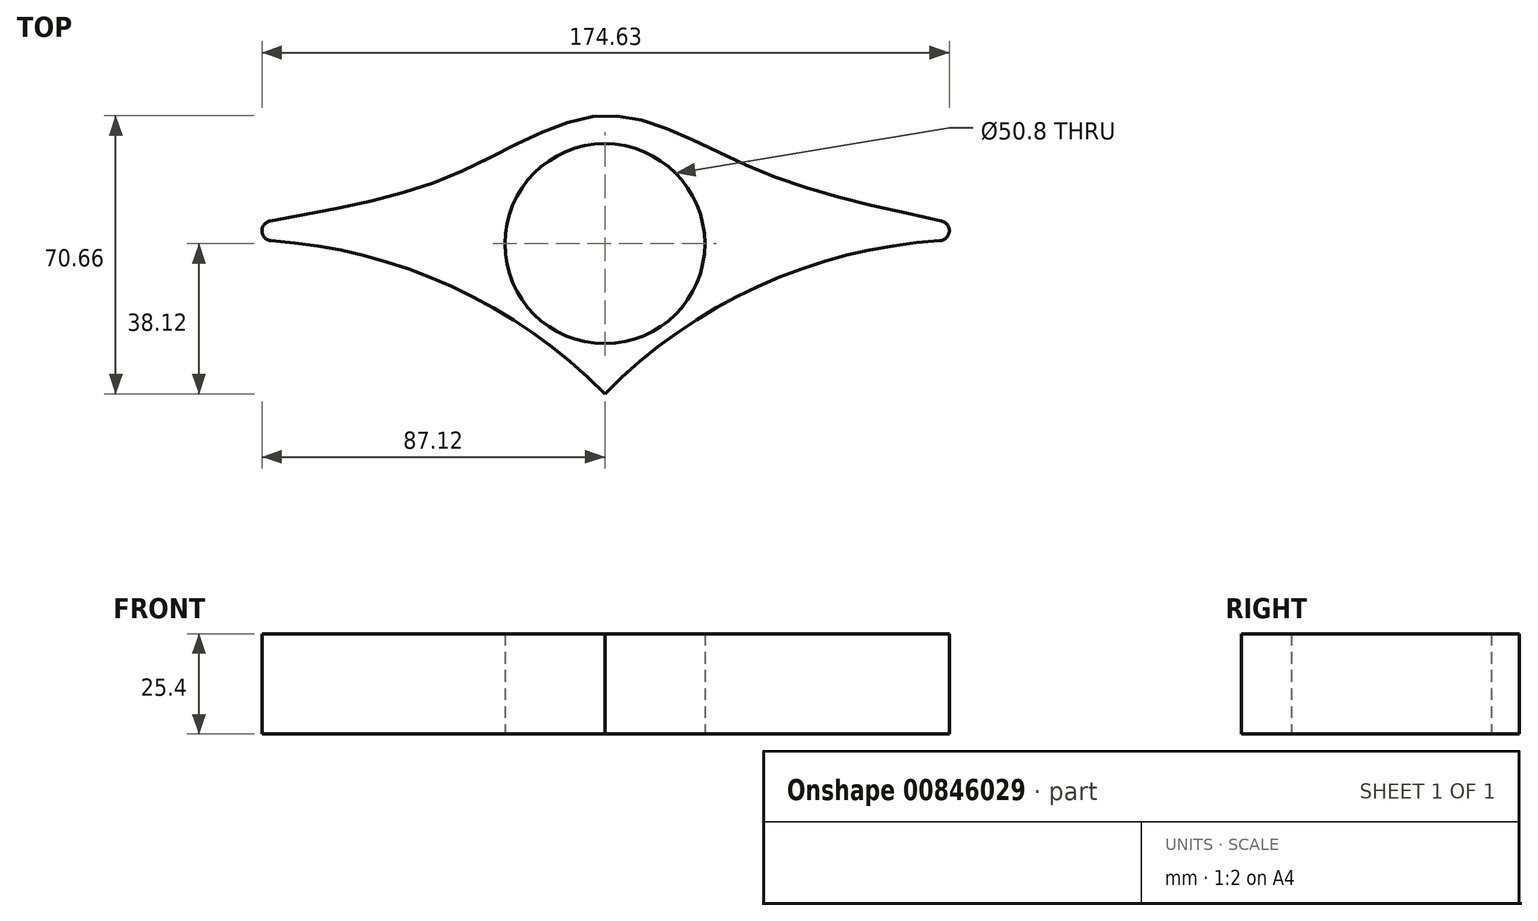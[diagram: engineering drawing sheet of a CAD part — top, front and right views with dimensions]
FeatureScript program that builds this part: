
annotation { "Feature Type Name" : "Feature", "Feature Type Description" : "" }
export const myFeature = defineFeature(function(context is Context, id is Id, definition is map)
    precondition{}
    {
        {
            var Q0;
            Q0=qCreatedBy(makeId("Top.planeOp"),FACE);
            var sketch = newSketch(context, id + "F0", { "sketchPlane" : qUnion([Q0])});
            skPoint(sketch, "E0.middle", {"position": v(0, 0) * mm});
            skCircle(sketch, "E1", {"center": v(0, 0) * mm, "radius": 25.4 * mm});
            skPoint(sketch, "E0.bottom.start.orphan", {"position": v(-220.64, 111.79) * mm});
            skPoint(sketch, "E2.orphan", {"position": v(220.64, 111.79) * mm});
            skArc(sketch, "E3", {"start": v(0, -38.12) * mm, "mid": v(-50.5, -6.2) * mm, "end": v(-109.93, 0) * mm});
            skArc(sketch, "E4.MirrorCS", {"start": v(0, -38.12) * mm, "mid": v(50.5, -6.2) * mm, "end": v(109.93, 0) * mm});
            skFitSpline(sketch, "E5", {"points": [v(-109.93, 0) * mm, v(-42.7, 15.8) * mm, v(0, 32.52) * mm, v(41.55, 17.64) * mm, v(109.93, 0) * mm], "startDerivative": vector(264.5, 77.18) * mm, "endDerivative": vector(256.83, -69.23) * mm});
            skSolve(sketch);
        }
        {
            var Q0;
            Q0 = qSketchRegion(id + "F0", true);
            extrude(context, id + "F1", {"entities" : qUnion([Q0]), "depth" : 25.4 * mm, "offsetDistance" : 25.4 * mm});
        }
        {
            var Q0;
            Q0=makeQuery(id+"F1.opExtrude","SWEPT_EDGE",EDGE,{"disambiguationData":[OSD([sQuery(id+"F0.wireOp",EDGE,"E3"),sQuery(id+"F0.wireOp",EDGE,"E5")])]});
            var Q1;
            Q1=makeQuery(id+"F1.opExtrude","SWEPT_EDGE",EDGE,{"disambiguationData":[OSD([sQuery(id+"F0.wireOp",EDGE,"E4.MirrorCS"),sQuery(id+"F0.wireOp",EDGE,"E5")])]});
            fillet(context, id + "F2", {"entities" : qUnion([Q0, Q1]), "radius" : 2.54 * mm, "tangentPropagation" : true, "allowEdgeOverflow" : false});
        }
    });
